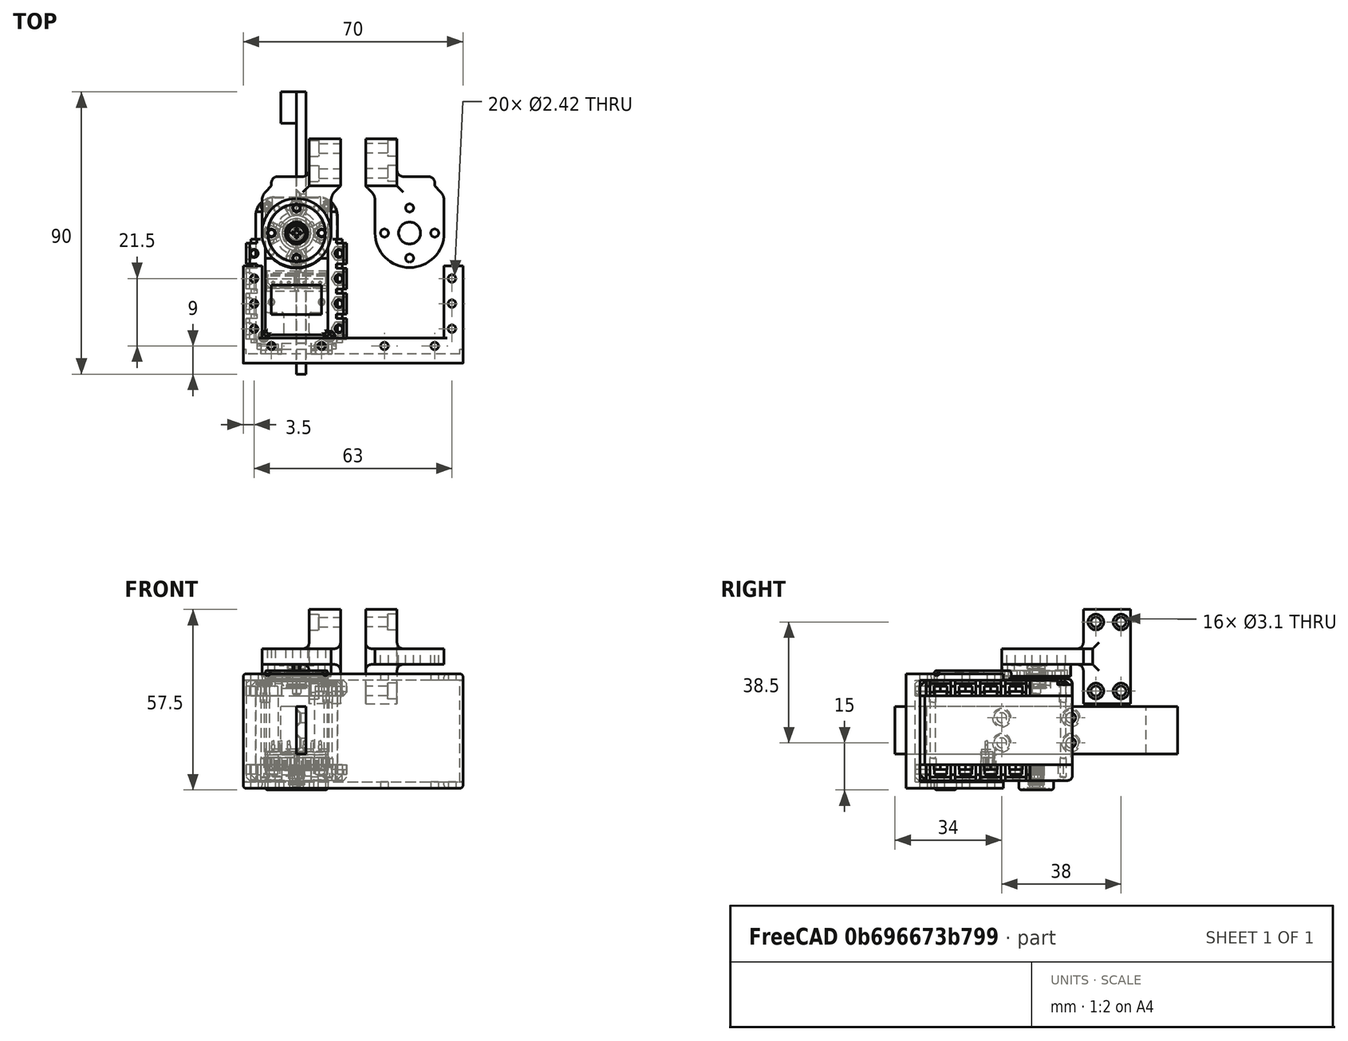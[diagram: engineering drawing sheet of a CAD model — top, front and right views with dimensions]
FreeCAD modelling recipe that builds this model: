
FCSTD DOCUMENT  (FreeCAD 1.1R20260414 (Git shallow))
Label: Unnamed
License: All rights reserved
LicenseURL: https://en.wikipedia.org/wiki/All_rights_reserved
objects: Sketcher::SketchObject×26, Part::Feature×22, PartDesign::Pad×16, App::Point×10, PartDesign::Hole×9, App::Link×8, PartDesign::Fillet×7, App::FeaturePython×7, PartDesign::Body×5, App::Part×4, PartDesign::ShapeBinder×3, PartDesign::PolarPattern×2, PartDesign::Pocket×1, Assembly::JointGroup×1, Assembly::AssemblyObject×1
note: 185 computed .brp shape members not serialized (recipe doc carries the construction recipe); baked Part::Feature solids carry a one-line shape summary decoded from their .brp
EXTERNAL_REF file=../card/Unnamed1.FCStd obj=Body

FEATURE [Part::Feature] Part__Feature  label="PRT0001"
  shape: bbox 32 x 50.5 x 38 mm, 671 faces (baked)
FEATURE [Part::Feature] Part__Feature001  label="PRT0002"
  Placement = pos=(0,0,-2) rot=(0,0,1;3.14159rad)
  shape: bbox 7.033 x 7.036 x 5.513 mm, 32 faces (baked)
FEATURE [Part::Feature] Part__Feature002  label="PRT0003"
  Placement = pos=(9.5,8.5,14.5) rot=(0,0.707107,0.707107;3.14159rad)
  shape: bbox 4.1 x 4.088 x 30.71 mm, 30 faces (baked)
FEATURE [Part::Feature] Part__Feature003  label="PRT0004"
  Placement = pos=(-9.5,8.5,14.5) rot=(0,0.707107,0.707107;3.14159rad)
  shape: bbox 4.1 x 4.088 x 30.71 mm, 30 faces (baked)
FEATURE [Part::Feature] Part__Feature004  label="PRT0005"
  Placement = pos=(10.5,-33,14.5) rot=(0,0.707107,0.707107;3.14159rad)
  shape: bbox 4.1 x 4.088 x 30.71 mm, 30 faces (baked)
FEATURE [Part::Feature] Part__Feature005  label="PRT0006"
  Placement = pos=(-10.5,-33,14.5) rot=(0,0.707107,0.707107;3.14159rad)
  shape: bbox 4.1 x 4.088 x 30.71 mm, 30 faces (baked)
FEATURE [Part::Feature] Part__Feature006  label="PRT0007"
  Placement = pos=(5.05,-15.19,-9.75) rot=(-1,0,0;1.5708rad)
  shape: bbox 9.902 x 4.902 x 9.405 mm, 93 faces (baked)
FEATURE [Part::Feature] Part__Feature007  label="PRT0008"
  Placement = pos=(-4.95,-15.19,-9.75) rot=(-1,0,0;1.5708rad)
  shape: bbox 9.902 x 4.902 x 9.405 mm, 93 faces (baked)
FEATURE [Part::Feature] Part__Feature008  label="PRT0009"
  Placement = pos=(0,0,-18.4) rot=(0,0.707107,0.707107;3.14159rad)
  shape: bbox 4.984 x 4.984 x 7 mm, 133 faces (baked)
FEATURE [Part::Feature] Part__Feature009  label="PRT0010"
  Placement = pos=(0,0,19.16) rot=(0,0,1;1.5708rad)
  shape: bbox 22 x 22 x 6.702 mm, 170 faces (baked)
FEATURE [Part::Feature] Part__Feature010  label="PRT0011"
  Placement = pos=(0,0,19.48) rot=(0,0.707107,0.707107;3.14159rad)
  shape: bbox 7.815 x 6.706 x 9.6 mm, 27 faces (baked)
FEATURE [App::Part] ASM0002_ASM
  Group = -> [Part__Feature,Part__Feature001,Part__Feature002,Part__Feature003,Part__Feature004,Part__Feature005,Part__Feature006,Part__Feature007,Part__Feature008,Part__Feature009,Part__Feature010]
  Origin = -> Origin
FEATURE [App::Point] Origin001
  Role = Origin
FEATURE [App::Part] ASM0001_ASM
  Group = -> [ASM0002_ASM]
  Origin = -> Origin002
FEATURE [App::Point] Origin003
  Role = Origin
FEATURE [App::Point] Origin005  label="Origin006"
  Role = Origin
FEATURE [PartDesign::ShapeBinder] CopyPart__Feature009
  Placement = pos=(0,0,19.16) rot=(0,0,1;1.5708rad)
  TraceSupport = false
FEATURE [Sketcher::SketchObject] Sketch
  ArcFitTolerance = 1e-06
  AttachmentSupport = -> [CopyPart__Feature009]
  ExternalTypes = [0]
  FullyConstrained = true
  MakeInternals = false
  MapMode = 5
  Placement = pos=(0,0,21) rot=(0,0,1;1.5708rad)
  _ExternalGeoVersion = 1
  sketch-geometry (4):
    g0: LineSegment StartX=-2e-15 StartY=-11 StartZ=0 EndX=12 EndY=-11 EndZ=0
    g1: LineSegment StartX=12 StartY=-11 StartZ=0 EndX=12 EndY=11 EndZ=0
    g2: LineSegment StartX=12 StartY=11 StartZ=0 EndX=-3.6e-15 EndY=11 EndZ=0
    g3: ArcOfCircle CenterX=0 CenterY=5e-16 CenterZ=0 NormalX=0 NormalY=0 NormalZ=1 AngleXU=0 Radius=11 StartAngle=1.5708 EndAngle=4.71239
  constraints (12):
    c: Coincident(g0,g1)
    c: Coincident(g1,g2)
    c: Horizontal(g0)
    c: Horizontal(g2)
    c: Vertical(g1)
    c: Distance(g1,g0) = 12
    c: Distance(g0,g2) = 22
    c: PointOnObject(g0,g-2)
    c: Distance(g-1,g0) = 11
    c: Tangent(g0,g3) = -1.5708
    c: Coincident(g3,g2)
    c: Angle(g3) = 3.14159
FEATURE [PartDesign::Pad] Pad
  Direction = (0,0,1)
  Length = 5
  Length2 = 10
  Placement = pos=(0,0,19.16) rot=(0,0,1;1.5708rad)
  Profile = -> Sketch
  ReferenceAxis = -> Sketch [N_Axis]
  Refine = true
  SideType = 0
  Suppressed = false
  Type = 0
  Type2 = 0
FEATURE [Sketcher::SketchObject] Sketch001
  ArcFitTolerance = 1e-06
  AttachmentSupport = -> [Pad]
  ExternalTypes = [0]
  FullyConstrained = true
  MakeInternals = false
  MapMode = 5
  Placement = pos=(0,0,26) rot=(0,0,1;1.5708rad)
  _ExternalGeoVersion = 1
  sketch-geometry (1):
    g0: Circle CenterX=-8 CenterY=0 CenterZ=0 NormalX=0 NormalY=0 NormalZ=1 AngleXU=0 Radius=1.1
  constraints (3):
    c: Diameter(g0) = 2.2
    c: PointOnObject(g0,g-1)
    c: Distance(g0,g-2) = 8
FEATURE [PartDesign::Hole] Hole
  BaseFeature = -> Pad
  BaseProfileType = 7
  CustomThreadClearance = 0
  Depth = 5
  DepthType = 0
  Diameter = 2.552
  DrillForDepth = false
  DrillPoint = 1
  DrillPointAngle = 118
  HoleCutCountersinkAngle = 90
  HoleCutCustomValues = false
  HoleCutDepth = 0
  HoleCutDiameter = 0
  HoleCutType = 0
  ModelThread = false
  Placement = pos=(0,0,19.16) rot=(0,0,1;1.5708rad)
  Profile = -> Sketch001
  Refine = true
  Suppressed = false
  Tapered = false
  TaperedAngle = 90
  ThreadClass = 0
  ThreadDepth = 5
  ThreadDepthType = 0
  ThreadDiameter = 2.2
  ThreadDirection = 0
  ThreadFit = 2
  ThreadSize = 7
  ThreadType = 1
  Threaded = false
  UseCustomThreadClearance = false
FEATURE [PartDesign::PolarPattern] PolarPattern
  Angle = 360
  Axis = -> Sketch001 [N_Axis]
  BaseFeature = -> Hole
  Mode = 0
  Occurrences = 4
  Offset = 120
  Originals = -> [Hole]
  Placement = pos=(0,0,19.16) rot=(0,0,1;1.5708rad)
  Refine = true
  SpacingPattern = [0]
  Spacings = [-1,-1,-1]
  Suppressed = false
  TransformMode = 0
FEATURE [Sketcher::SketchObject] Sketch002
  ArcFitTolerance = 1e-06
  AttachmentSupport = -> [PolarPattern]
  ExternalTypes = [0]
  FullyConstrained = true
  MakeInternals = false
  MapMode = 5
  Placement = pos=(0,0,26) rot=(0,0,1;1.5708rad)
  _ExternalGeoVersion = 1
  sketch-geometry (1):
    g0: Circle CenterX=0 CenterY=0 CenterZ=0 NormalX=0 NormalY=0 NormalZ=1 AngleXU=0 Radius=3
  constraints (2):
    c: Diameter(g0) = 6
    c: Coincident(g0,g-1)
FEATURE [PartDesign::Hole] Hole001
  BaseFeature = -> PolarPattern
  BaseProfileType = 7
  CustomThreadClearance = 0
  Depth = 5
  DepthType = 0
  Diameter = 7
  DrillForDepth = false
  DrillPoint = 1
  DrillPointAngle = 118
  HoleCutCountersinkAngle = 90
  HoleCutCustomValues = false
  HoleCutDepth = 0
  HoleCutDiameter = 0
  HoleCutType = 0
  ModelThread = false
  Placement = pos=(0,0,19.16) rot=(0,0,1;1.5708rad)
  Profile = -> Sketch002
  Refine = true
  Suppressed = false
  Tapered = false
  TaperedAngle = 90
  ThreadClass = 0
  ThreadDepth = 5
  ThreadDepthType = 0
  ThreadDiameter = 6
  ThreadDirection = 0
  ThreadFit = 2
  ThreadSize = 14
  ThreadType = 1
  Threaded = false
  UseCustomThreadClearance = false
FEATURE [App::Point] Origin007  label="Origin009"
  Role = Origin
FEATURE [App::Point] Origin009  label="Origin011"
  Role = Origin
FEATURE [Part::Feature] Part__Feature011  label="PRT0012"
  shape: bbox 32 x 50.5 x 38 mm, 671 faces (baked)
FEATURE [Part::Feature] Part__Feature012  label="PRT0013"
  Placement = pos=(0,0,-2) rot=(0,0,1;3.14159rad)
  shape: bbox 7.033 x 7.036 x 5.513 mm, 32 faces (baked)
FEATURE [Part::Feature] Part__Feature013  label="PRT0014"
  Placement = pos=(9.5,8.5,14.5) rot=(0,0.707107,0.707107;3.14159rad)
  shape: bbox 4.1 x 4.088 x 30.71 mm, 30 faces (baked)
FEATURE [Part::Feature] Part__Feature014  label="PRT0015"
  Placement = pos=(-9.5,8.5,14.5) rot=(0,0.707107,0.707107;3.14159rad)
  shape: bbox 4.1 x 4.088 x 30.71 mm, 30 faces (baked)
FEATURE [Part::Feature] Part__Feature015  label="PRT0016"
  Placement = pos=(10.5,-33,14.5) rot=(0,0.707107,0.707107;3.14159rad)
  shape: bbox 4.1 x 4.088 x 30.71 mm, 30 faces (baked)
FEATURE [Part::Feature] Part__Feature016  label="PRT0017"
  Placement = pos=(-10.5,-33,14.5) rot=(0,0.707107,0.707107;3.14159rad)
  shape: bbox 4.1 x 4.088 x 30.71 mm, 30 faces (baked)
FEATURE [Part::Feature] Part__Feature017  label="PRT0018"
  Placement = pos=(5.05,-15.19,-9.75) rot=(-1,0,0;1.5708rad)
  shape: bbox 9.902 x 4.902 x 9.405 mm, 93 faces (baked)
FEATURE [Part::Feature] Part__Feature018  label="PRT0019"
  Placement = pos=(-4.95,-15.19,-9.75) rot=(-1,0,0;1.5708rad)
  shape: bbox 9.902 x 4.902 x 9.405 mm, 93 faces (baked)
FEATURE [Part::Feature] Part__Feature019  label="PRT0020"
  Placement = pos=(0,0,-18.4) rot=(0,0.707107,0.707107;3.14159rad)
  shape: bbox 4.984 x 4.984 x 7 mm, 133 faces (baked)
FEATURE [Part::Feature] Part__Feature020  label="PRT0021"
  Placement = pos=(0,0,19.16) rot=(0,0,1;1.5708rad)
  shape: bbox 22 x 22 x 6.702 mm, 170 faces (baked)
FEATURE [Part::Feature] Part__Feature021  label="PRT0022"
  Placement = pos=(0,0,19.48) rot=(0,0.707107,0.707107;3.14159rad)
  shape: bbox 7.815 x 6.706 x 9.6 mm, 27 faces (baked)
FEATURE [App::Part] ASM0002_ASM001
  Group = -> [Part__Feature011,Part__Feature012,Part__Feature013,Part__Feature014,Part__Feature015,Part__Feature016,Part__Feature017,Part__Feature018,Part__Feature019,Part__Feature020,Part__Feature021]
  Origin = -> Origin006
FEATURE [App::Part] ASM0001_ASM001
  Group = -> [ASM0002_ASM001]
  Origin = -> Origin008
  Placement = pos=(36,0,0) rot=(0,0,1;0rad)
FEATURE [PartDesign::ShapeBinder] CopyPart__Feature
  TraceSupport = false
FEATURE [App::Point] Origin013  label="Origin015"
  Role = Origin
FEATURE [Sketcher::SketchObject] Sketch012
  ArcFitTolerance = 1e-06
  AttachmentSupport = -> [CopyPart__Feature]
  ExternalTypes = [0]
  FullyConstrained = true
  MakeInternals = false
  MapMode = 5
  Placement = pos=(0,-38.5,0) rot=(1,0,0;1.5708rad)
  _ExternalGeoVersion = 1
  sketch-geometry (4):
    g0: LineSegment StartX=-17 StartY=18 StartZ=0 EndX=-17 EndY=-18.5 EndZ=0
    g1: LineSegment StartX=-17 StartY=-18.5 StartZ=0 EndX=53 EndY=-18.5 EndZ=0
    g2: LineSegment StartX=53 StartY=-18.5 StartZ=0 EndX=53 EndY=18 EndZ=0
    g3: LineSegment StartX=53 StartY=18 StartZ=0 EndX=-17 EndY=18 EndZ=0
  constraints (12):
    c: Coincident(g0,g1)
    c: Coincident(g1,g2)
    c: Coincident(g2,g3)
    c: Coincident(g3,g0)
    c: Vertical(g0)
    c: Vertical(g2)
    c: Horizontal(g1)
    c: Horizontal(g3)
    c: DistanceY(g0,g0) = 36.5
    c: Distance(g-2,g0) = 17
    c: DistanceX(g1,g1) = 70
    c: Distance(g-1,g3) = 18
FEATURE [PartDesign::Pad] Pad006
  Direction = (0,-1,2e-16)
  Length = 3
  Length2 = 10
  Profile = -> Sketch012
  ReferenceAxis = -> Sketch012 [N_Axis]
  Refine = true
  SideType = 0
  Suppressed = false
  Type = 0
  Type2 = 0
FEATURE [Sketcher::SketchObject] Sketch013
  ArcFitTolerance = 1e-06
  AttachmentSupport = -> [Pad006]
  ExternalTypes = [0]
  FullyConstrained = true
  MakeInternals = false
  MapMode = 5
  Placement = pos=(0,-38.5,1.5e-14) rot=(0,0.707107,0.707107;3.14159rad)
  _ExternalGeoVersion = 1
  sketch-geometry (4):
    g0: LineSegment StartX=17 StartY=18 StartZ=0 EndX=-53 EndY=18 EndZ=0
    g1: LineSegment StartX=-53 StartY=18 StartZ=0 EndX=-53 EndY=16 EndZ=0
    g2: LineSegment StartX=-53 StartY=16 StartZ=0 EndX=17 EndY=16 EndZ=0
    g3: LineSegment StartX=17 StartY=16 StartZ=0 EndX=17 EndY=18 EndZ=0
  constraints (12):
    c: Coincident(g0,g1)
    c: Coincident(g1,g2)
    c: Coincident(g2,g3)
    c: Coincident(g3,g0)
    c: Horizontal(g0)
    c: Horizontal(g2)
    c: Vertical(g1)
    c: Vertical(g3)
    c: Distance(g1,g3) = 70
    c: Distance(g0,g2) = 2
    c: Distance(g-1,g2) = 16
    c: Distance(g-2,g3) = 17
FEATURE [PartDesign::Pad] Pad007
  BaseFeature = -> Pad006
  Direction = (0,1,-2e-16)
  Length = 5
  Length2 = 10
  Profile = -> Sketch013
  ReferenceAxis = -> Sketch013 [N_Axis]
  Refine = true
  SideType = 0
  Suppressed = false
  Type = 0
  Type2 = 0
FEATURE [Sketcher::SketchObject] Sketch014
  ArcFitTolerance = 1e-06
  AttachmentSupport = -> [Pad007]
  ExternalTypes = [0]
  FullyConstrained = true
  MakeInternals = false
  MapMode = 5
  Placement = pos=(0,-38.5,1.5e-14) rot=(0,0.707107,0.707107;3.14159rad)
  _ExternalGeoVersion = 1
  sketch-geometry (4):
    g0: LineSegment StartX=17 StartY=-18.5 StartZ=0 EndX=17 EndY=-16.5 EndZ=0
    g1: LineSegment StartX=17 StartY=-16.5 StartZ=0 EndX=-53 EndY=-16.5 EndZ=0
    g2: LineSegment StartX=-53 StartY=-16.5 StartZ=0 EndX=-53 EndY=-18.5 EndZ=0
    g3: LineSegment StartX=-53 StartY=-18.5 StartZ=0 EndX=17 EndY=-18.5 EndZ=0
  constraints (12):
    c: Coincident(g0,g1)
    c: Coincident(g1,g2)
    c: Coincident(g2,g3)
    c: Coincident(g3,g0)
    c: Vertical(g0)
    c: Vertical(g2)
    c: Horizontal(g1)
    c: Horizontal(g3)
    c: Distance(g0,g2) = 70
    c: Distance(g1,g3) = 2
    c: Distance(g-2,g0) = 17
    c: Distance(g-1,g3) = 18.5
FEATURE [PartDesign::Pad] Pad008
  BaseFeature = -> Pad007
  Direction = (0,1,-2e-16)
  Length = 5
  Length2 = 10
  Profile = -> Sketch014
  ReferenceAxis = -> Sketch014 [N_Axis]
  Refine = true
  SideType = 0
  Suppressed = false
  Type = 0
  Type2 = 0
FEATURE [Sketcher::SketchObject] Sketch015
  ArcFitTolerance = 1e-06
  AttachmentSupport = -> [Pad008]
  ExternalTypes = [0,0]
  FullyConstrained = true
  MakeInternals = false
  MapMode = 5
  Placement = pos=(0,-33.5,1.19e-13) rot=(0,0.707107,0.707107;3.14159rad)
  _ExternalGeoVersion = 1
  sketch-geometry (16):
    g0: LineSegment StartX=17 StartY=16 StartZ=0 EndX=17 EndY=18 EndZ=0
    g1: LineSegment StartX=17 StartY=18 StartZ=0 EndX=11 EndY=18 EndZ=0
    g2: LineSegment StartX=11 StartY=18 StartZ=0 EndX=11 EndY=16 EndZ=0
    g3: LineSegment StartX=11 StartY=16 StartZ=0 EndX=17 EndY=16 EndZ=0
    g4: LineSegment StartX=-53 StartY=16 StartZ=0 EndX=-47 EndY=16 EndZ=0
    g5: LineSegment StartX=-47 StartY=16 StartZ=0 EndX=-47 EndY=18 EndZ=0
    g6: LineSegment StartX=-47 StartY=18 StartZ=0 EndX=-53 EndY=18 EndZ=0
    g7: LineSegment StartX=-53 StartY=18 StartZ=0 EndX=-53 EndY=16 EndZ=0
    g8: LineSegment StartX=-53 StartY=-16.5 StartZ=0 EndX=-53 EndY=-18.5 EndZ=0
    g9: LineSegment StartX=-53 StartY=-18.5 StartZ=0 EndX=-47 EndY=-18.5 EndZ=0
    g10: LineSegment StartX=-47 StartY=-18.5 StartZ=0 EndX=-47 EndY=-16.5 EndZ=0
    g11: LineSegment StartX=-47 StartY=-16.5 StartZ=0 EndX=-53 EndY=-16.5 EndZ=0
    g12: LineSegment StartX=17 StartY=-16.5 StartZ=0 EndX=11 EndY=-16.5 EndZ=0
    g13: LineSegment StartX=11 StartY=-16.5 StartZ=0 EndX=11 EndY=-18.5 EndZ=0
    g14: LineSegment StartX=11 StartY=-18.5 StartZ=0 EndX=17 EndY=-18.5 EndZ=0
    g15: LineSegment StartX=17 StartY=-18.5 StartZ=0 EndX=17 EndY=-16.5 EndZ=0
  constraints (48):
    c: Coincident(g0,g1)
    c: Coincident(g1,g2)
    c: Coincident(g2,g3)
    c: Coincident(g3,g0)
    c: Vertical(g0)
    c: Vertical(g2)
    c: Horizontal(g1)
    c: Horizontal(g3)
    c: Distance(g0,g2) = 6
    c: Distance(g1,g3) = 2
    c: Distance(g-1,g3) = 16
    c: Distance(g-2,g0) = 17
    c: Coincident(g4,g5)
    c: Coincident(g5,g6)
    c: Coincident(g6,g7)
    c: Coincident(g7,g4)
    c: Horizontal(g4)
    c: Horizontal(g6)
    c: Vertical(g5)
    c: Vertical(g7)
    c: Distance(g-1,g4) = 16
    c: Distance(g7,g7) = 2
    c: Distance(g-2,g7) = 53
    c: Distance(g6,g6) = 6
    c: Coincident(g8,g9)
    c: Coincident(g9,g10)
    c: Coincident(g10,g11)
    c: Coincident(g11,g8)
    c: Vertical(g8)
    c: Vertical(g10)
    c: Horizontal(g9)
    c: Horizontal(g11)
    c: Coincident(g12,g13)
    c: Coincident(g13,g14)
    c: Coincident(g14,g15)
    c: Coincident(g15,g12)
    c: Horizontal(g12)
    c: Horizontal(g14)
    c: Vertical(g13)
    c: Vertical(g15)
    c: Distance(g-2,g15) = 17
    c: Distance(g-1,g12) = 16.5
    c: Distance(g13,g13) = 2
    c: Distance(g14,g14) = 6
    c: Distance(g-1,g11) = 16.5
    c: Distance(g-2,g8) = 53
    c: Distance(g9,g9) = 6
    c: Distance(g10,g10) = 2
FEATURE [PartDesign::Pad] Pad009
  BaseFeature = -> Pad008
  Direction = (0,1,-3.6e-15)
  Length = 23
  Length2 = 10
  Profile = -> Sketch015
  ReferenceAxis = -> Sketch015 [N_Axis]
  Refine = true
  SideType = 0
  Suppressed = false
  Type = 0
  Type2 = 0
FEATURE [Sketcher::SketchObject] Sketch016
  ArcFitTolerance = 1e-06
  AttachmentSupport = -> [Pad009]
  ExternalTypes = [0,0]
  FullyConstrained = true
  MakeInternals = false
  MapMode = 5
  Placement = pos=(0,-38.5,1.5e-14) rot=(0,0.707107,0.707107;3.14159rad)
  _ExternalGeoVersion = 1
  sketch-geometry (8):
    g0: LineSegment StartX=-53 StartY=16 StartZ=0 EndX=-53 EndY=-16.5 EndZ=0
    g1: LineSegment StartX=-53 StartY=-16.5 StartZ=0 EndX=-52 EndY=-16.5 EndZ=0
    g2: LineSegment StartX=-52 StartY=-16.5 StartZ=0 EndX=-52 EndY=16 EndZ=0
    g3: LineSegment StartX=-52 StartY=16 StartZ=0 EndX=-53 EndY=16 EndZ=0
    g4: LineSegment StartX=17 StartY=16 StartZ=0 EndX=16 EndY=16 EndZ=0
    g5: LineSegment StartX=16 StartY=16 StartZ=0 EndX=16 EndY=-16.5 EndZ=0
    g6: LineSegment StartX=16 StartY=-16.5 StartZ=0 EndX=17 EndY=-16.5 EndZ=0
    g7: LineSegment StartX=17 StartY=-16.5 StartZ=0 EndX=17 EndY=16 EndZ=0
  constraints (24):
    c: Coincident(g0,g1)
    c: Coincident(g1,g2)
    c: Coincident(g2,g3)
    c: Coincident(g3,g0)
    c: Vertical(g0)
    c: Vertical(g2)
    c: Horizontal(g1)
    c: Horizontal(g3)
    c: Distance(g0,g2) = 1
    c: Distance(g1,g3) = 32.5
    c: Distance(g-1,g3) = 16
    c: Distance(g-2,g0) = 53
    c: Coincident(g4,g5)
    c: Coincident(g5,g6)
    c: Coincident(g6,g7)
    c: Coincident(g7,g4)
    c: Horizontal(g4)
    c: Horizontal(g6)
    c: Vertical(g5)
    c: Vertical(g7)
    c: Distance(g-2,g7) = 17
    c: Distance(g-1,g4) = 16
    c: Distance(g7,g7) = 32.5
    c: Distance(g6,g6) = 1
FEATURE [PartDesign::Pad] Pad010
  BaseFeature = -> Pad009
  Direction = (0,1,-2e-16)
  Length = 1.5
  Length2 = 10
  Profile = -> Sketch016
  ReferenceAxis = -> Sketch016 [N_Axis]
  Refine = true
  SideType = 0
  Suppressed = false
  Type = 0
  Type2 = 0
FEATURE [PartDesign::Fillet] Fillet008
  Base = -> Pad010 [Edge47,Edge45,Edge20,Edge18,Edge5,Edge23,Edge41,Edge43]
  BaseFeature = -> Pad010
  Radius = 1
  Refine = true
  SupportTransform = false
  Suppressed = false
  UseAllEdges = false
FEATURE [Sketcher::SketchObject] Sketch017
  ArcFitTolerance = 1e-06
  AttachmentSupport = -> [Fillet008]
  ExternalTypes = [0]
  FullyConstrained = true
  MakeInternals = false
  MapMode = 5
  Placement = pos=(0,-1.22e-14,18) rot=(0,0,1;0rad)
  _ExternalGeoVersion = 1
  sketch-geometry (10):
    g0: Circle CenterX=-13.5 CenterY=-14.5 CenterZ=0 NormalX=0 NormalY=0 NormalZ=1 AngleXU=0 Radius=1.1
    g1: Circle CenterX=-13.5 CenterY=-22.5 CenterZ=0 NormalX=0 NormalY=0 NormalZ=1 AngleXU=0 Radius=1.1
    g2: Circle CenterX=-13.5 CenterY=-30.5 CenterZ=0 NormalX=0 NormalY=0 NormalZ=1 AngleXU=0 Radius=1.1
    g3: Circle CenterX=49.5 CenterY=-14.5 CenterZ=0 NormalX=0 NormalY=0 NormalZ=1 AngleXU=0 Radius=1.1
    g4: Circle CenterX=49.5 CenterY=-22.5 CenterZ=0 NormalX=0 NormalY=0 NormalZ=1 AngleXU=0 Radius=1.1
    g5: Circle CenterX=49.5 CenterY=-30.5 CenterZ=0 NormalX=0 NormalY=0 NormalZ=1 AngleXU=0 Radius=1.1
    g6: Circle CenterX=-8 CenterY=-36 CenterZ=0 NormalX=0 NormalY=0 NormalZ=1 AngleXU=0 Radius=1.1
    g7: Circle CenterX=8 CenterY=-36 CenterZ=0 NormalX=0 NormalY=0 NormalZ=1 AngleXU=0 Radius=1.1
    g8: Circle CenterX=44 CenterY=-36 CenterZ=0 NormalX=0 NormalY=0 NormalZ=1 AngleXU=0 Radius=1.1
    g9: Circle CenterX=28 CenterY=-36 CenterZ=0 NormalX=0 NormalY=0 NormalZ=1 AngleXU=0 Radius=1.1
  constraints (30):
    c: Diameter(g0) = 2.2
    c: Equal(g0,g1)
    c: Equal(g2,g1)
    c: Distance(g0,g-2) = 13.5
    c: DistanceY(g0,g-1) = 14.5
    c: Distance(g1,g0) = 8
    c: Distance(g1,g-2) = 13.5
    c: Distance(g2,g1) = 8
    c: Distance(g2,g-2) = 13.5
    c: Diameter(g3) = 2.2
    c: DistanceX(g-1,g3) = 49.5
    c: DistanceY(g3,g-1) = 14.5
    c: Equal(g3,g4)
    c: Equal(g4,g5)
    c: Distance(g4,g3) = 8
    c: Distance(g5,g4) = 8
    c: Distance(g4,g-2) = 49.5
    c: Distance(g5,g-2) = 49.5
    c: Equal(g2,g6)
    c: Distance(g6,g-2) = 8
    c: DistanceY(g6,g-1) = 36
    c: Equal(g7,g6)
    c: DistanceX(g6,g7) = 16
    c: Distance(g7,g-1) = 36
    c: Equal(g9,g5)
    c: Equal(g8,g5)
    c: DistanceX(g9,g8) = 16
    c: Distance(g9,g-1) = 36
    c: Distance(g8,g-1) = 36
    c: Distance(g9,g-2) = 28
FEATURE [PartDesign::Hole] Hole006
  BaseFeature = -> Fillet008
  BaseProfileType = 7
  CustomThreadClearance = 0
  Depth = 40
  DepthType = 0
  Diameter = 2.42
  DrillForDepth = false
  DrillPoint = 1
  DrillPointAngle = 118
  HoleCutCountersinkAngle = 90
  HoleCutCustomValues = false
  HoleCutDepth = 0
  HoleCutDiameter = 0
  HoleCutType = 0
  ModelThread = false
  Profile = -> Sketch017
  Refine = true
  Suppressed = false
  Tapered = false
  TaperedAngle = 90
  ThreadClass = 0
  ThreadDepth = 40
  ThreadDepthType = 0
  ThreadDiameter = 2.2
  ThreadDirection = 0
  ThreadFit = 0
  ThreadSize = 7
  ThreadType = 1
  Threaded = false
  UseCustomThreadClearance = false
FEATURE [PartDesign::Body] Body002
  AllowCompound = true
  Group = -> [CopyPart__Feature,Sketch012,Pad006,Sketch013,Pad007,Sketch014,Pad008,Sketch015,Pad009,Sketch016,Pad010,Fillet008,Sketch017,Hole006]
  Origin = -> Origin012
  Tip = -> Hole006
FEATURE [Sketcher::SketchObject] Sketch018
  ArcFitTolerance = 1e-06
  AttachmentSupport = -> [Hole001]
  ExternalTypes = [0]
  FullyConstrained = true
  MakeInternals = false
  MapMode = 5
  Placement = pos=(0,0,26) rot=(0,0,1;1.5708rad)
  _ExternalGeoVersion = 1
  sketch-geometry (4):
    g0: LineSegment StartX=12 StartY=11 StartZ=0 EndX=15 EndY=8.00374 EndZ=0
    g1: LineSegment StartX=15 StartY=8.00374 StartZ=0 EndX=15 EndY=-13.9963 EndZ=0
    g2: LineSegment StartX=15 StartY=-13.9963 StartZ=0 EndX=12 EndY=-11 EndZ=0
    g3: LineSegment StartX=12 StartY=11 StartZ=0 EndX=12 EndY=-11 EndZ=0
  constraints (12):
    c: Coincident(g0,g1)
    c: Vertical(g1)
    c: Coincident(g1,g2)
    c: Coincident(g0,g3)
    c: Coincident(g3,g2)
    c: Vertical(g3)
    c: Distance(g1,g1) = 22
    c: Distance(g0,g0) = 4.24
    c: Equal(g1,g3)
    c: Distance(g-2,g1) = 15
    c: Distance(g-2,g3) = 12
    c: Distance(g0,g-1) = 11
FEATURE [PartDesign::Pad] Pad011
  BaseFeature = -> Hole001
  Direction = (0,0,1)
  Length = 5
  Length2 = 10
  Placement = pos=(0,0,19.16) rot=(0,0,1;1.5708rad)
  Profile = -> Sketch018
  ReferenceAxis = -> Sketch018 [N_Axis]
  Refine = true
  Reversed = true
  SideType = 0
  Suppressed = false
  Type = 0
  Type2 = 0
FEATURE [Sketcher::SketchObject] Sketch019
  ArcFitTolerance = 1e-06
  AttachmentSupport = -> [Pad011]
  ExternalTypes = [0,0,0]
  FullyConstrained = true
  MakeInternals = false
  MapMode = 5
  Placement = pos=(0,0,26) rot=(0,0,1;1.5708rad)
  _ExternalGeoVersion = 1
  sketch-geometry (4):
    g0: LineSegment StartX=15 StartY=8 StartZ=0 EndX=15 EndY=-14 EndZ=0
    g1: LineSegment StartX=15 StartY=-14 StartZ=0 EndX=18 EndY=-14 EndZ=0
    g2: LineSegment StartX=18 StartY=-14 StartZ=0 EndX=18 EndY=8 EndZ=0
    g3: LineSegment StartX=18 StartY=8 StartZ=0 EndX=15 EndY=8 EndZ=0
  constraints (12):
    c: Coincident(g0,g1)
    c: Coincident(g1,g2)
    c: Coincident(g2,g3)
    c: Coincident(g3,g0)
    c: Vertical(g0)
    c: Vertical(g2)
    c: Horizontal(g1)
    c: Horizontal(g3)
    c: Distance(g0,g2) = 3
    c: Distance(g1,g3) = 22
    c: Distance(g-2,g2) = 18
    c: Distance(g1,g-1) = 14
FEATURE [PartDesign::Pad] Pad012
  BaseFeature = -> Pad011
  Direction = (0,0,1)
  Length = 5
  Length2 = 10
  Placement = pos=(0,0,19.16) rot=(0,0,1;1.5708rad)
  Profile = -> Sketch019
  ReferenceAxis = -> Sketch019 [N_Axis]
  Refine = true
  Reversed = true
  SideType = 0
  Suppressed = false
  Type = 0
  Type2 = 0
FEATURE [Sketcher::SketchObject] Sketch020
  ArcFitTolerance = 1e-06
  AttachmentSupport = -> [Pad012]
  ExternalTypes = [0]
  FullyConstrained = true
  MakeInternals = false
  MapMode = 5
  Placement = pos=(14,-4.7e-15,19.16) rot=(0.57735,0.57735,0.57735;2.0944rad)
  _ExternalGeoVersion = 1
  sketch-geometry (4):
    g0: LineSegment StartX=15 StartY=19.34 StartZ=0 EndX=15 EndY=-10.66 EndZ=0
    g1: LineSegment StartX=15 StartY=-10.66 StartZ=0 EndX=30 EndY=-10.66 EndZ=0
    g2: LineSegment StartX=30 StartY=-10.66 StartZ=0 EndX=30 EndY=19.34 EndZ=0
    g3: LineSegment StartX=30 StartY=19.34 StartZ=0 EndX=15 EndY=19.34 EndZ=0
  constraints (12):
    c: Coincident(g0,g1)
    c: Coincident(g1,g2)
    c: Coincident(g2,g3)
    c: Coincident(g3,g0)
    c: Vertical(g0)
    c: Vertical(g2)
    c: Horizontal(g1)
    c: Horizontal(g3)
    c: Distance(g0,g2) = 15
    c: Distance(g1,g3) = 30
    c: Distance(g-1,g1) = 10.66
    c: Distance(g-2,g0) = 15
FEATURE [PartDesign::Pad] Pad013
  BaseFeature = -> Pad012
  Direction = (1,0,0)
  Length = 10
  Length2 = 10
  Placement = pos=(0,0,19.16) rot=(0,0,1;1.5708rad)
  Profile = -> Sketch020
  ReferenceAxis = -> Sketch020 [N_Axis]
  Refine = true
  Reversed = true
  SideType = 0
  Suppressed = false
  Type = 0
  Type2 = 0
FEATURE [PartDesign::Fillet] Fillet
  Base = -> Pad013 [Edge42,Edge40,Edge28,Edge12]
  BaseFeature = -> Pad013
  Placement = pos=(0,0,19.16) rot=(0,0,1;1.5708rad)
  Radius = 2
  Refine = true
  SupportTransform = false
  Suppressed = false
  UseAllEdges = false
FEATURE [PartDesign::Fillet] Fillet009
  Base = -> Fillet [Edge31,Edge29,Edge6,Edge4]
  BaseFeature = -> Fillet
  Placement = pos=(0,0,19.16) rot=(0,0,1;1.5708rad)
  Radius = 2
  Refine = true
  SupportTransform = false
  Suppressed = false
  UseAllEdges = false
FEATURE [PartDesign::Fillet] Fillet010
  Base = -> Fillet009 [Edge29,Edge19]
  BaseFeature = -> Fillet009
  Placement = pos=(0,0,19.16) rot=(0,0,1;1.5708rad)
  Radius = 4
  Refine = true
  SupportTransform = false
  Suppressed = false
  UseAllEdges = false
FEATURE [Sketcher::SketchObject] Sketch021
  ArcFitTolerance = 1e-06
  AttachmentSupport = -> [Fillet010]
  ExternalTypes = [0,0,0]
  FullyConstrained = true
  MakeInternals = false
  MapMode = 5
  Placement = pos=(4,-4e-16,19.16) rot=(0.57735,-0.57735,-0.57735;2.0944rad)
  _ExternalGeoVersion = 1
  sketch-geometry (4):
    g0: Circle CenterX=-19 CenterY=15.34 CenterZ=0 NormalX=0 NormalY=0 NormalZ=1 AngleXU=0 Radius=1.1
    g1: Circle CenterX=-27 CenterY=15.34 CenterZ=0 NormalX=0 NormalY=0 NormalZ=1 AngleXU=0 Radius=1.1
    g2: Circle CenterX=-19 CenterY=-6.66 CenterZ=0 NormalX=0 NormalY=0 NormalZ=1 AngleXU=0 Radius=1.1
    g3: Circle CenterX=-27 CenterY=-6.66 CenterZ=0 NormalX=0 NormalY=0 NormalZ=1 AngleXU=0 Radius=1.1
  constraints (12):
    c: Diameter(g0) = 2.2
    c: Equal(g1,g0)
    c: Equal(g3,g1)
    c: Equal(g2,g3)
    c: DistanceX(g1,g0) = 8
    c: DistanceX(g3,g2) = 8
    c: Distance(g0,g-1) = 15.34
    c: Distance(g0,g-2) = 19
    c: Distance(g1,g-1) = 15.34
    c: Distance(g2,g-2) = 19
    c: Distance(g2,g-1) = 6.66
    c: Distance(g3,g-1) = 6.66
FEATURE [PartDesign::Hole] Hole007
  BaseFeature = -> Fillet010
  BaseProfileType = 7
  CustomThreadClearance = 0
  Depth = 10
  DepthType = 0
  Diameter = 3.1
  DrillForDepth = false
  DrillPoint = 0
  DrillPointAngle = 118
  HoleCutCountersinkAngle = 90
  HoleCutCustomValues = false
  HoleCutDepth = 3
  HoleCutDiameter = 5
  HoleCutType = 1
  ModelThread = false
  Placement = pos=(0,0,19.16) rot=(0,0,1;1.5708rad)
  Profile = -> Sketch021
  Refine = true
  Suppressed = false
  Tapered = false
  TaperedAngle = 90
  ThreadClass = 0
  ThreadDepth = 10
  ThreadDepthType = 0
  ThreadDiameter = 2.5
  ThreadDirection = 0
  ThreadFit = 2
  ThreadSize = 8
  ThreadType = 1
  Threaded = false
  UseCustomThreadClearance = false
FEATURE [PartDesign::Body] Body
  AllowCompound = true
  Group = -> [CopyPart__Feature009,Sketch,Pad,Sketch001,Hole,PolarPattern,Sketch002,Hole001,Sketch018,Pad011,Sketch019,Pad012,Sketch020,Pad013,Fillet,Fillet009,Fillet010,Sketch021,Hole007]
  Origin = -> Origin004
  Tip = -> Hole007
FEATURE [PartDesign::ShapeBinder] CopyPart__Feature010
  Placement = pos=(0,0,19.16) rot=(0,0,1;1.5708rad)
  TraceSupport = false
FEATURE [App::Point] Origin015  label="Origin017"
  Role = Origin
FEATURE [Sketcher::SketchObject] Sketch022
  ArcFitTolerance = 1e-06
  AttachmentSupport = -> [CopyPart__Feature010]
  ExternalTypes = [0]
  FullyConstrained = true
  MakeInternals = false
  MapMode = 5
  Placement = pos=(0,0,21) rot=(0,0,1;1.5708rad)
  _ExternalGeoVersion = 1
  sketch-geometry (4):
    g0: LineSegment StartX=-2e-15 StartY=-11 StartZ=0 EndX=12 EndY=-11 EndZ=0
    g1: LineSegment StartX=12 StartY=-11 StartZ=0 EndX=12 EndY=11 EndZ=0
    g2: LineSegment StartX=12 StartY=11 StartZ=0 EndX=-3.6e-15 EndY=11 EndZ=0
    g3: ArcOfCircle CenterX=0 CenterY=5e-16 CenterZ=0 NormalX=0 NormalY=0 NormalZ=1 AngleXU=0 Radius=11 StartAngle=1.5708 EndAngle=4.71239
  constraints (12):
    c: Coincident(g0,g1)
    c: Coincident(g1,g2)
    c: Horizontal(g0)
    c: Horizontal(g2)
    c: Vertical(g1)
    c: Distance(g1,g0) = 12
    c: Distance(g0,g2) = 22
    c: PointOnObject(g0,g-2)
    c: Distance(g-1,g0) = 11
    c: Tangent(g0,g3) = -1.5708
    c: Coincident(g3,g2)
    c: Angle(g3) = 3.14159
FEATURE [PartDesign::Pad] Pad014
  Direction = (0,0,1)
  Length = 5
  Length2 = 10
  Placement = pos=(0,0,19.16) rot=(0,0,1;1.5708rad)
  Profile = -> Sketch022
  ReferenceAxis = -> Sketch022 [N_Axis]
  Refine = true
  SideType = 0
  Suppressed = false
  Type = 0
  Type2 = 0
FEATURE [Sketcher::SketchObject] Sketch023
  ArcFitTolerance = 1e-06
  AttachmentSupport = -> [Pad014]
  ExternalTypes = [0]
  FullyConstrained = true
  MakeInternals = false
  MapMode = 5
  Placement = pos=(0,0,26) rot=(0,0,1;1.5708rad)
  _ExternalGeoVersion = 1
  sketch-geometry (1):
    g0: Circle CenterX=-8 CenterY=0 CenterZ=0 NormalX=0 NormalY=0 NormalZ=1 AngleXU=0 Radius=1.1
  constraints (3):
    c: Diameter(g0) = 2.2
    c: PointOnObject(g0,g-1)
    c: Distance(g0,g-2) = 8
FEATURE [PartDesign::Hole] Hole008
  BaseFeature = -> Pad014
  BaseProfileType = 7
  CustomThreadClearance = 0
  Depth = 5
  DepthType = 0
  Diameter = 2.552
  DrillForDepth = false
  DrillPoint = 1
  DrillPointAngle = 118
  HoleCutCountersinkAngle = 90
  HoleCutCustomValues = false
  HoleCutDepth = 0
  HoleCutDiameter = 0
  HoleCutType = 0
  ModelThread = false
  Placement = pos=(0,0,19.16) rot=(0,0,1;1.5708rad)
  Profile = -> Sketch023
  Refine = true
  Suppressed = false
  Tapered = false
  TaperedAngle = 90
  ThreadClass = 0
  ThreadDepth = 5
  ThreadDepthType = 0
  ThreadDiameter = 2.2
  ThreadDirection = 0
  ThreadFit = 2
  ThreadSize = 7
  ThreadType = 1
  Threaded = false
  UseCustomThreadClearance = false
FEATURE [PartDesign::PolarPattern] PolarPattern001
  Angle = 360
  Axis = -> Sketch023 [N_Axis]
  BaseFeature = -> Hole008
  Mode = 0
  Occurrences = 4
  Offset = 120
  Originals = -> [Hole008]
  Placement = pos=(0,0,19.16) rot=(0,0,1;1.5708rad)
  Refine = true
  SpacingPattern = [0]
  Spacings = [-1,-1,-1]
  Suppressed = false
  TransformMode = 0
FEATURE [Sketcher::SketchObject] Sketch024
  ArcFitTolerance = 1e-06
  AttachmentSupport = -> [PolarPattern001]
  ExternalTypes = [0]
  FullyConstrained = true
  MakeInternals = false
  MapMode = 5
  Placement = pos=(0,0,26) rot=(0,0,1;1.5708rad)
  _ExternalGeoVersion = 1
  sketch-geometry (1):
    g0: Circle CenterX=0 CenterY=0 CenterZ=0 NormalX=0 NormalY=0 NormalZ=1 AngleXU=0 Radius=3
  constraints (2):
    c: Diameter(g0) = 6
    c: Coincident(g0,g-1)
FEATURE [PartDesign::Hole] Hole009
  BaseFeature = -> PolarPattern001
  BaseProfileType = 7
  CustomThreadClearance = 0
  Depth = 5
  DepthType = 0
  Diameter = 7
  DrillForDepth = false
  DrillPoint = 1
  DrillPointAngle = 118
  HoleCutCountersinkAngle = 90
  HoleCutCustomValues = false
  HoleCutDepth = 0
  HoleCutDiameter = 0
  HoleCutType = 0
  ModelThread = false
  Placement = pos=(0,0,19.16) rot=(0,0,1;1.5708rad)
  Profile = -> Sketch024
  Refine = true
  Suppressed = false
  Tapered = false
  TaperedAngle = 90
  ThreadClass = 0
  ThreadDepth = 5
  ThreadDepthType = 0
  ThreadDiameter = 6
  ThreadDirection = 0
  ThreadFit = 2
  ThreadSize = 14
  ThreadType = 1
  Threaded = false
  UseCustomThreadClearance = false
FEATURE [Sketcher::SketchObject] Sketch025
  ArcFitTolerance = 1e-06
  AttachmentSupport = -> [Hole009]
  ExternalTypes = [0]
  FullyConstrained = true
  MakeInternals = false
  MapMode = 5
  Placement = pos=(0,0,26) rot=(0,0,1;1.5708rad)
  _ExternalGeoVersion = 1
  sketch-geometry (4):
    g0: LineSegment StartX=12 StartY=11 StartZ=0 EndX=15 EndY=8.00374 EndZ=0
    g1: LineSegment StartX=15 StartY=8.00374 StartZ=0 EndX=15 EndY=-13.9963 EndZ=0
    g2: LineSegment StartX=15 StartY=-13.9963 StartZ=0 EndX=12 EndY=-11 EndZ=0
    g3: LineSegment StartX=12 StartY=11 StartZ=0 EndX=12 EndY=-11 EndZ=0
  constraints (12):
    c: Coincident(g0,g1)
    c: Vertical(g1)
    c: Coincident(g1,g2)
    c: Coincident(g0,g3)
    c: Coincident(g3,g2)
    c: Vertical(g3)
    c: Distance(g1,g1) = 22
    c: Distance(g0,g0) = 4.24
    c: Equal(g1,g3)
    c: Distance(g-2,g1) = 15
    c: Distance(g-2,g3) = 12
    c: Distance(g0,g-1) = 11
FEATURE [PartDesign::Pad] Pad015
  BaseFeature = -> Hole009
  Direction = (0,0,1)
  Length = 5
  Length2 = 10
  Placement = pos=(0,0,19.16) rot=(0,0,1;1.5708rad)
  Profile = -> Sketch025
  ReferenceAxis = -> Sketch025 [N_Axis]
  Refine = true
  Reversed = true
  SideType = 0
  Suppressed = false
  Type = 0
  Type2 = 0
FEATURE [Sketcher::SketchObject] Sketch026
  ArcFitTolerance = 1e-06
  AttachmentSupport = -> [Pad015]
  ExternalTypes = [0,0,0]
  FullyConstrained = true
  MakeInternals = false
  MapMode = 5
  Placement = pos=(0,0,26) rot=(0,0,1;1.5708rad)
  _ExternalGeoVersion = 1
  sketch-geometry (4):
    g0: LineSegment StartX=15 StartY=8 StartZ=0 EndX=15 EndY=-14 EndZ=0
    g1: LineSegment StartX=15 StartY=-14 StartZ=0 EndX=18 EndY=-14 EndZ=0
    g2: LineSegment StartX=18 StartY=-14 StartZ=0 EndX=18 EndY=8 EndZ=0
    g3: LineSegment StartX=18 StartY=8 StartZ=0 EndX=15 EndY=8 EndZ=0
  constraints (12):
    c: Coincident(g0,g1)
    c: Coincident(g1,g2)
    c: Coincident(g2,g3)
    c: Coincident(g3,g0)
    c: Vertical(g0)
    c: Vertical(g2)
    c: Horizontal(g1)
    c: Horizontal(g3)
    c: Distance(g0,g2) = 3
    c: Distance(g1,g3) = 22
    c: Distance(g-2,g2) = 18
    c: Distance(g1,g-1) = 14
FEATURE [PartDesign::Pad] Pad016
  BaseFeature = -> Pad015
  Direction = (0,0,1)
  Length = 5
  Length2 = 10
  Placement = pos=(0,0,19.16) rot=(0,0,1;1.5708rad)
  Profile = -> Sketch026
  ReferenceAxis = -> Sketch026 [N_Axis]
  Refine = true
  Reversed = true
  SideType = 0
  Suppressed = false
  Type = 0
  Type2 = 0
FEATURE [Sketcher::SketchObject] Sketch027
  ArcFitTolerance = 1e-06
  AttachmentSupport = -> [Pad016]
  ExternalTypes = [0]
  FullyConstrained = true
  MakeInternals = false
  MapMode = 5
  Placement = pos=(14,-4.7e-15,19.16) rot=(0.57735,0.57735,0.57735;2.0944rad)
  _ExternalGeoVersion = 1
  sketch-geometry (4):
    g0: LineSegment StartX=15 StartY=19.34 StartZ=0 EndX=15 EndY=-10.66 EndZ=0
    g1: LineSegment StartX=15 StartY=-10.66 StartZ=0 EndX=30 EndY=-10.66 EndZ=0
    g2: LineSegment StartX=30 StartY=-10.66 StartZ=0 EndX=30 EndY=19.34 EndZ=0
    g3: LineSegment StartX=30 StartY=19.34 StartZ=0 EndX=15 EndY=19.34 EndZ=0
  constraints (12):
    c: Coincident(g0,g1)
    c: Coincident(g1,g2)
    c: Coincident(g2,g3)
    c: Coincident(g3,g0)
    c: Vertical(g0)
    c: Vertical(g2)
    c: Horizontal(g1)
    c: Horizontal(g3)
    c: Distance(g0,g2) = 15
    c: Distance(g1,g3) = 30
    c: Distance(g-1,g1) = 10.66
    c: Distance(g-2,g0) = 15
FEATURE [PartDesign::Pad] Pad017
  BaseFeature = -> Pad016
  Direction = (1,0,0)
  Length = 10
  Length2 = 10
  Placement = pos=(0,0,19.16) rot=(0,0,1;1.5708rad)
  Profile = -> Sketch027
  ReferenceAxis = -> Sketch027 [N_Axis]
  Refine = true
  Reversed = true
  SideType = 0
  Suppressed = false
  Type = 0
  Type2 = 0
FEATURE [PartDesign::Fillet] Fillet011
  Base = -> Pad017 [Edge42,Edge40,Edge28,Edge12]
  BaseFeature = -> Pad017
  Placement = pos=(0,0,19.16) rot=(0,0,1;1.5708rad)
  Radius = 2
  Refine = true
  SupportTransform = false
  Suppressed = false
  UseAllEdges = false
FEATURE [PartDesign::Fillet] Fillet012
  Base = -> Fillet011 [Edge31,Edge29,Edge6,Edge4]
  BaseFeature = -> Fillet011
  Placement = pos=(0,0,19.16) rot=(0,0,1;1.5708rad)
  Radius = 2
  Refine = true
  SupportTransform = false
  Suppressed = false
  UseAllEdges = false
FEATURE [PartDesign::Fillet] Fillet013
  Base = -> Fillet012 [Edge29,Edge19]
  BaseFeature = -> Fillet012
  Placement = pos=(0,0,19.16) rot=(0,0,1;1.5708rad)
  Radius = 4
  Refine = true
  SupportTransform = false
  Suppressed = false
  UseAllEdges = false
FEATURE [Sketcher::SketchObject] Sketch028
  ArcFitTolerance = 1e-06
  AttachmentSupport = -> [Fillet013]
  ExternalTypes = [0,0,0]
  FullyConstrained = true
  MakeInternals = false
  MapMode = 5
  Placement = pos=(4,-4e-16,19.16) rot=(0.57735,-0.57735,-0.57735;2.0944rad)
  _ExternalGeoVersion = 1
  sketch-geometry (4):
    g0: Circle CenterX=-19 CenterY=15.34 CenterZ=0 NormalX=0 NormalY=0 NormalZ=1 AngleXU=0 Radius=1.1
    g1: Circle CenterX=-27 CenterY=15.34 CenterZ=0 NormalX=0 NormalY=0 NormalZ=1 AngleXU=0 Radius=1.1
    g2: Circle CenterX=-19 CenterY=-6.66 CenterZ=0 NormalX=0 NormalY=0 NormalZ=1 AngleXU=0 Radius=1.1
    g3: Circle CenterX=-27 CenterY=-6.66 CenterZ=0 NormalX=0 NormalY=0 NormalZ=1 AngleXU=0 Radius=1.1
  constraints (12):
    c: Diameter(g0) = 2.2
    c: Equal(g1,g0)
    c: Equal(g3,g1)
    c: Equal(g2,g3)
    c: DistanceX(g1,g0) = 8
    c: DistanceX(g3,g2) = 8
    c: Distance(g0,g-1) = 15.34
    c: Distance(g0,g-2) = 19
    c: Distance(g1,g-1) = 15.34
    c: Distance(g2,g-2) = 19
    c: Distance(g2,g-1) = 6.66
    c: Distance(g3,g-1) = 6.66
FEATURE [PartDesign::Hole] Hole010
  BaseFeature = -> Fillet013
  BaseProfileType = 7
  CustomThreadClearance = 0
  Depth = 10
  DepthType = 0
  Diameter = 3.1
  DrillForDepth = false
  DrillPoint = 0
  DrillPointAngle = 118
  HoleCutCountersinkAngle = 90
  HoleCutCustomValues = false
  HoleCutDepth = 3
  HoleCutDiameter = 5
  HoleCutType = 1
  ModelThread = false
  Placement = pos=(0,0,19.16) rot=(0,0,1;1.5708rad)
  Profile = -> Sketch028
  Refine = true
  Suppressed = false
  Tapered = false
  TaperedAngle = 90
  ThreadClass = 0
  ThreadDepth = 10
  ThreadDepthType = 0
  ThreadDiameter = 2.5
  ThreadDirection = 0
  ThreadFit = 2
  ThreadSize = 8
  ThreadType = 1
  Threaded = false
  UseCustomThreadClearance = false
FEATURE [PartDesign::Body] Body003
  AllowCompound = true
  Group = -> [CopyPart__Feature010,Sketch022,Pad014,Sketch023,Hole008,PolarPattern001,Sketch024,Hole009,Sketch025,Pad015,Sketch026,Pad016,Sketch027,Pad017,Fillet011,Fillet012,Fillet013,Sketch028,Hole010]
  Origin = -> Origin014
  Placement = pos=(36,0,47) rot=(0,-1,0;3.14159rad)
  Tip = -> Hole010
FEATURE [App::Point] Origin017  label="Origin019"
  Role = Origin
FEATURE [Sketcher::SketchObject] Sketch029
  ArcFitTolerance = 1e-06
  AttachmentSupport = -> [Origin016]
  ExternalTypes = [0]
  FullyConstrained = true
  MakeInternals = false
  MapMode = 5
  Placement = pos=(0,0,0) rot=(0.57735,0.57735,0.57735;2.0944rad)
  _ExternalGeoVersion = 1
  sketch-geometry (5):
    g0: LineSegment StartX=-45 StartY=-7.5 StartZ=0 EndX=45 EndY=-7.5 EndZ=0
    g1: LineSegment StartX=45 StartY=-7.5 StartZ=0 EndX=45 EndY=7.5 EndZ=0
    g2: LineSegment StartX=45 StartY=7.5 StartZ=0 EndX=-45 EndY=7.5 EndZ=0
    g3: LineSegment StartX=-45 StartY=7.5 StartZ=0 EndX=-45 EndY=-7.5 EndZ=0
    g4: GeomPoint [constr] X=0 Y=0 Z=0
  constraints (12):
    c: Coincident(g0,g1)
    c: Coincident(g1,g2)
    c: Coincident(g2,g3)
    c: Coincident(g3,g0)
    c: Horizontal(g0)
    c: Horizontal(g2)
    c: Vertical(g1)
    c: Vertical(g3)
    c: Symmetric(g2,g0,g4)
    c: Distance(g1,g3) = 90
    c: Distance(g0,g2) = 15
    c: Coincident(g4,g-1)
FEATURE [PartDesign::Pad] Pad018
  Direction = (1,0,0)
  Length = 3
  Length2 = 10
  Profile = -> Sketch029
  ReferenceAxis = -> Sketch029 [N_Axis]
  Refine = true
  SideType = 0
  Suppressed = false
  Type = 0
  Type2 = 0
FEATURE [Sketcher::SketchObject] Sketch030
  ArcFitTolerance = 1e-06
  AttachmentSupport = -> [Pad018]
  ExternalGeometry = -> [Pad018]
  ExternalTypes = [0,0]
  FullyConstrained = true
  MakeInternals = false
  MapMode = 5
  Placement = pos=(0,0,0) rot=(0.57735,-0.57735,-0.57735;2.0944rad)
  _ExternalGeoVersion = 1
  sketch-geometry (4):
    g0: Circle CenterX=-11 CenterY=4 CenterZ=0 NormalX=0 NormalY=0 NormalZ=1 AngleXU=0 Radius=1.1
    g1: Circle CenterX=-11 CenterY=-4 CenterZ=0 NormalX=0 NormalY=0 NormalZ=1 AngleXU=0 Radius=1.1
    g2: Circle CenterX=11 CenterY=4 CenterZ=0 NormalX=0 NormalY=0 NormalZ=1 AngleXU=0 Radius=1.1
    g3: Circle CenterX=11 CenterY=-4 CenterZ=0 NormalX=0 NormalY=0 NormalZ=1 AngleXU=0 Radius=1.1
  constraints (12):
    c: Diameter(g0) = 2.2
    c: Equal(g0,g1)
    c: Distance(g0,g1) = 8
    c: Distance(g0,g-2) = 11
    c: Distance(g1,g-2) = 11
    c: Distance(g0,g-1) = 4
    c: Equal(g1,g3)
    c: Equal(g3,g2)
    c: Distance(g3,g-2) = 11
    c: Distance(g2,g-2) = 11
    c: Distance(g2,g-1) = 4
    c: Distance(g2,g3) = 8
FEATURE [PartDesign::Hole] Hole011
  BaseFeature = -> Pad018
  BaseProfileType = 7
  CustomThreadClearance = 0
  Depth = 3
  DepthType = 0
  Diameter = 3.1
  DrillForDepth = false
  DrillPoint = 0
  DrillPointAngle = 118
  HoleCutCountersinkAngle = 90
  HoleCutCustomValues = false
  HoleCutDepth = 2.5
  HoleCutDiameter = 5
  HoleCutType = 2
  ModelThread = false
  Profile = -> Sketch030
  Refine = true
  Suppressed = false
  Tapered = false
  TaperedAngle = 90
  ThreadClass = 0
  ThreadDepth = 3
  ThreadDepthType = 0
  ThreadDiameter = 2.5
  ThreadDirection = 0
  ThreadFit = 2
  ThreadSize = 8
  ThreadType = 1
  Threaded = false
  UseCustomThreadClearance = false
FEATURE [Sketcher::SketchObject] Sketch031
  ArcFitTolerance = 1e-06
  AttachmentSupport = -> [Hole011]
  ExternalTypes = [0]
  FullyConstrained = true
  MakeInternals = false
  MapMode = 5
  Placement = pos=(0,0,0) rot=(0.57735,-0.57735,-0.57735;2.0944rad)
  _ExternalGeoVersion = 1
  sketch-geometry (4):
    g0: LineSegment StartX=-45 StartY=7.5 StartZ=0 EndX=-45 EndY=-7.5 EndZ=0
    g1: LineSegment StartX=-45 StartY=-7.5 StartZ=0 EndX=-35 EndY=-7.5 EndZ=0
    g2: LineSegment StartX=-35 StartY=-7.5 StartZ=0 EndX=-35 EndY=7.5 EndZ=0
    g3: LineSegment StartX=-35 StartY=7.5 StartZ=0 EndX=-45 EndY=7.5 EndZ=0
  constraints (12):
    c: Coincident(g0,g1)
    c: Coincident(g1,g2)
    c: Coincident(g2,g3)
    c: Coincident(g3,g0)
    c: Vertical(g0)
    c: Vertical(g2)
    c: Horizontal(g1)
    c: Horizontal(g3)
    c: Distance(g0,g2) = 10
    c: Distance(g1,g3) = 15
    c: Distance(g-1,g3) = 7.5
    c: Distance(g-2,g0) = 45
FEATURE [PartDesign::Pad] Pad019
  BaseFeature = -> Hole011
  Direction = (-1,0,0)
  Length = 5
  Length2 = 10
  Profile = -> Sketch031
  ReferenceAxis = -> Sketch031 [N_Axis]
  Refine = true
  SideType = 0
  Suppressed = false
  Type = 0
  Type2 = 0
FEATURE [PartDesign::Body] Body004
  AllowCompound = true
  Group = -> [Sketch029,Pad018,Sketch030,Hole011,Sketch031,Pad019]
  Origin = -> Origin016
  Tip = -> Pad019
FEATURE [App::Point] Origin019  label="Origin021"
  Role = Origin
FEATURE [Sketcher::SketchObject] Sketch032
  ArcFitTolerance = 1e-06
  AttachmentSupport = -> [Origin018]
  ExternalTypes = [0]
  FullyConstrained = true
  MakeInternals = false
  MapMode = 5
  Placement = pos=(0,0,0) rot=(0.57735,0.57735,0.57735;2.0944rad)
  _ExternalGeoVersion = 1
  sketch-geometry (5):
    g0: LineSegment StartX=-45 StartY=-7.5 StartZ=0 EndX=45 EndY=-7.5 EndZ=0
    g1: LineSegment StartX=45 StartY=-7.5 StartZ=0 EndX=45 EndY=7.5 EndZ=0
    g2: LineSegment StartX=45 StartY=7.5 StartZ=0 EndX=-45 EndY=7.5 EndZ=0
    g3: LineSegment StartX=-45 StartY=7.5 StartZ=0 EndX=-45 EndY=-7.5 EndZ=0
    g4: GeomPoint [constr] X=0 Y=0 Z=0
  constraints (12):
    c: Coincident(g0,g1)
    c: Coincident(g1,g2)
    c: Coincident(g2,g3)
    c: Coincident(g3,g0)
    c: Horizontal(g0)
    c: Horizontal(g2)
    c: Vertical(g1)
    c: Vertical(g3)
    c: Symmetric(g2,g0,g4)
    c: Distance(g1,g3) = 90
    c: Distance(g0,g2) = 15
    c: Coincident(g4,g-1)
FEATURE [PartDesign::Pad] Pad020
  Direction = (1,0,0)
  Length = 3
  Length2 = 10
  Profile = -> Sketch032
  ReferenceAxis = -> Sketch032 [N_Axis]
  Refine = true
  SideType = 0
  Suppressed = false
  Type = 0
  Type2 = 0
FEATURE [Sketcher::SketchObject] Sketch033
  ArcFitTolerance = 1e-06
  AttachmentSupport = -> [Pad020]
  ExternalTypes = [0]
  FullyConstrained = true
  MakeInternals = false
  MapMode = 5
  Placement = pos=(0,0,0) rot=(0.57735,-0.57735,-0.57735;2.0944rad)
  _ExternalGeoVersion = 1
  sketch-geometry (4):
    g0: Circle CenterX=-11 CenterY=4 CenterZ=0 NormalX=0 NormalY=0 NormalZ=1 AngleXU=0 Radius=1.25
    g1: Circle CenterX=-11 CenterY=-4 CenterZ=0 NormalX=0 NormalY=0 NormalZ=1 AngleXU=0 Radius=1.25
    g2: Circle CenterX=11 CenterY=4 CenterZ=0 NormalX=0 NormalY=0 NormalZ=1 AngleXU=0 Radius=1.25
    g3: Circle CenterX=11 CenterY=-4 CenterZ=0 NormalX=0 NormalY=0 NormalZ=1 AngleXU=0 Radius=1.25
  constraints (12):
    c: Diameter(g0) = 2.5
    c: Equal(g0,g1)
    c: Equal(g1,g3)
    c: Equal(g3,g2)
    c: Distance(g0,g-1) = 4
    c: Distance(g0,g-2) = 11
    c: Distance(g1,g-2) = 11
    c: Distance(g1,g0) = 8
    c: Distance(g2,g-2) = 11
    c: Distance(g3,g-2) = 11
    c: Distance(g3,g2) = 8
    c: Distance(g2,g-1) = 4
FEATURE [PartDesign::Hole] Hole012
  BaseFeature = -> Pad020
  BaseProfileType = 7
  CustomThreadClearance = 0
  Depth = 3
  DepthType = 0
  Diameter = 3.1
  DrillForDepth = false
  DrillPoint = 0
  DrillPointAngle = 118
  HoleCutCountersinkAngle = 90
  HoleCutCustomValues = false
  HoleCutDepth = 2.95
  HoleCutDiameter = 5.9
  HoleCutType = 2
  ModelThread = false
  Profile = -> Sketch033
  Refine = true
  Suppressed = false
  Tapered = false
  TaperedAngle = 90
  ThreadClass = 0
  ThreadDepth = 3
  ThreadDepthType = 0
  ThreadDiameter = 2.5
  ThreadDirection = 0
  ThreadFit = 2
  ThreadSize = 8
  ThreadType = 1
  Threaded = false
  UseCustomThreadClearance = false
FEATURE [Sketcher::SketchObject] Sketch034
  ArcFitTolerance = 1e-06
  AttachmentSupport = -> [Hole012]
  ExternalTypes = [0]
  FullyConstrained = true
  MakeInternals = false
  MapMode = 5
  Placement = pos=(0,0,0) rot=(0.57735,-0.57735,-0.57735;2.0944rad)
  _ExternalGeoVersion = 1
  sketch-geometry (4):
    g0: LineSegment StartX=45 StartY=7.5 StartZ=0 EndX=35 EndY=7.5 EndZ=0
    g1: LineSegment StartX=35 StartY=7.5 StartZ=0 EndX=35 EndY=-7.5 EndZ=0
    g2: LineSegment StartX=35 StartY=-7.5 StartZ=0 EndX=45 EndY=-7.5 EndZ=0
    g3: LineSegment StartX=45 StartY=-7.5 StartZ=0 EndX=45 EndY=7.5 EndZ=0
  constraints (12):
    c: Coincident(g0,g1)
    c: Coincident(g1,g2)
    c: Coincident(g2,g3)
    c: Coincident(g3,g0)
    c: Horizontal(g0)
    c: Horizontal(g2)
    c: Vertical(g1)
    c: Vertical(g3)
    c: Distance(g1,g3) = 10
    c: Distance(g0,g2) = 15
    c: Distance(g-2,g1) = 35
    c: Distance(g-1,g0) = 7.5
FEATURE [PartDesign::Pocket] Pocket
  BaseFeature = -> Hole012
  Direction = (1,0,0)
  Length = 3
  Length2 = 5
  Profile = -> Sketch034
  ReferenceAxis = -> Sketch034 [N_Axis]
  Refine = true
  SideType = 0
  Suppressed = false
  Type = 0
  Type2 = 0
FEATURE [PartDesign::Body] Body005
  AllowCompound = true
  Group = -> [Sketch032,Pad020,Sketch033,Hole012,Sketch034,Pocket]
  Origin = -> Origin018
  Tip = -> Pocket
FEATURE [App::Point] Origin021  label="Origin024"
  Role = Origin
FEATURE [App::Link] Body006
  LinkPlacement = pos=(36,-8.06848e-06,-0.499997) rot=(1,0,0;3.14159rad)
  LinkedObject = -> Body002
  Placement = pos=(36,-8.06848e-06,-0.499997) rot=(1,0,0;3.14159rad)
FEATURE [App::FeaturePython] GroundedJoint  # Assembly grounded joint (typed FeaturePython)
  ObjectToGround = -> Body006
FEATURE [App::Link] ASM0001_ASM002
  LinkPlacement = pos=(72,-1.67271e-05,3.27024e-06) rot=(0,0,1;3.14159rad)
  LinkedObject = -> ASM0001_ASM001
  Placement = pos=(72,-1.67271e-05,3.27024e-06) rot=(0,0,1;3.14159rad)
FEATURE [App::Link] ASM0001_ASM003
  LinkPlacement = pos=(36,-8.14398e-06,3.27024e-06) rot=(0,0,1;3.14159rad)
  LinkedObject = -> ASM0001_ASM001
  Placement = pos=(36,-8.14398e-06,3.27024e-06) rot=(0,0,1;3.14159rad)
FEATURE [App::FeaturePython] Joint  label="Fixed"  # Assembly joint (typed FeaturePython)
  Angle = 0
  AngleMax = 0
  AngleMin = 0
  Detach1 = false
  Detach2 = false
  Distance = 0
  Distance2 = 0
  EnableAngleMax = false
  EnableAngleMin = false
  EnableLengthMax = false
  EnableLengthMin = false
  JointType = 0 (Fixed)
  LengthMax = 0
  LengthMin = 0
  Offset2 = pos=(0,0,0) rot=(0,0,-1;1.5708rad)
  Placement1 = pos=(13.5,-14.5,16) rot=(0,0,1;1.5708rad)
  Placement2 = pos=(-13.5,-14.5,-16.5) rot=(-0.707107,-0.707107,0;3.14159rad)
  Reference1 = -> ASM0001_ASM003 [ASM0002_ASM001.Part__Feature011.Edge800,ASM0002_ASM001.Part__Feature011.Edge800]
  Reference2 = -> Body006 [Edge112,Edge112]
  Suppressed = false
FEATURE [App::FeaturePython] Joint001  label="Fixed001"  # Assembly joint (typed FeaturePython)
  Angle = 0
  AngleMax = 0
  AngleMin = 0
  Detach1 = false
  Detach2 = false
  Distance = 0
  Distance2 = 0
  EnableAngleMax = false
  EnableAngleMin = false
  EnableLengthMax = false
  EnableLengthMin = false
  JointType = 0 (Fixed)
  LengthMax = 0
  LengthMin = 0
  Offset2 = pos=(0,0,0) rot=(0,0,-1;1.5708rad)
  Placement1 = pos=(-13.5,-14.5,16) rot=(0,0,1;1.5708rad)
  Placement2 = pos=(49.5,-14.5,-16.5) rot=(-0.707107,-0.707107,0;3.14159rad)
  Reference1 = -> ASM0001_ASM002 [ASM0002_ASM001.Part__Feature011.Edge812,ASM0002_ASM001.Part__Feature011.Edge812]
  Reference2 = -> Body006 [Edge107,Edge107]
  Suppressed = false
FEATURE [App::Link] Body007
  LinkPlacement = pos=(72,-1.67271e-05,3.27024e-06) rot=(0,0,1;3.1705rad)
  LinkedObject = -> Body
  Placement = pos=(72,-1.67271e-05,3.27024e-06) rot=(0,0,1;3.1705rad)
FEATURE [App::FeaturePython] Joint002  label="Revolute003"  # Assembly joint (typed FeaturePython)
  Angle = 0
  AngleMax = 0
  AngleMin = 0
  Detach1 = false
  Detach2 = false
  Distance = 0
  Distance2 = 0
  EnableAngleMax = false
  EnableAngleMin = false
  EnableLengthMax = false
  EnableLengthMin = false
  JointType = 1 (Revolute)
  LengthMax = 0
  LengthMin = 0
  Placement1 = pos=(0,0,1.84) rot=(0,0,-1;1.5708rad)
  Placement2 = pos=(1.42e-14,-4e-16,21) rot=(0,0,-1;4.71239rad)
  Reference1 = -> ASM0001_ASM002 [ASM0002_ASM001.Part__Feature020.Edge126,ASM0002_ASM001.Part__Feature020.Edge126]
  Reference2 = -> Body007 [Edge16,Edge16]
  Suppressed = false
FEATURE [App::Link] Body008
  LinkPlacement = pos=(36,-1.52408e-05,47) rot=(0.999864,0.01647,0;3.14159rad)
  LinkedObject = -> Body
  Placement = pos=(36,-1.52408e-05,47) rot=(0.999864,0.01647,0;3.14159rad)
FEATURE [App::FeaturePython] Joint003  label="Revolute004"  # Assembly joint (typed FeaturePython)
  Angle = 0
  AngleMax = 0
  AngleMin = 0
  Detach1 = false
  Detach2 = false
  Distance = 0
  Distance2 = 0
  EnableAngleMax = false
  EnableAngleMin = false
  EnableLengthMax = false
  EnableLengthMin = false
  JointType = 1 (Revolute)
  LengthMax = 0
  LengthMin = 0
  Placement1 = pos=(0,0,1.84) rot=(0,0,1;0rad)
  Placement2 = pos=(0,0,26) rot=(0,0,-1;4.71239rad)
  Reference1 = -> ASM0001_ASM003 [ASM0002_ASM001.Part__Feature020.Edge123,ASM0002_ASM001.Part__Feature020.Edge123]
  Reference2 = -> Body008 [Edge53,Edge53]
  Suppressed = false
FEATURE [App::Link] Body009
  LinkPlacement = pos=(53.7483,-22.4276,23.5) rot=(-0.011647,0.707059,0.707059;3.16488rad)
  LinkedObject = -> Body005
  Placement = pos=(53.7483,-22.4276,23.5) rot=(-0.011647,0.707059,0.707059;3.16488rad)
FEATURE [App::FeaturePython] Joint004  label="Fixed003"  # Assembly joint (typed FeaturePython)
  Angle = 0
  AngleMax = 0
  AngleMin = 0
  Detach1 = false
  Detach2 = false
  Distance = 0
  Distance2 = 0
  EnableAngleMax = false
  EnableAngleMin = false
  EnableLengthMax = false
  EnableLengthMin = false
  JointType = 0 (Fixed)
  LengthMax = 0
  LengthMin = 0
  Offset2 = pos=(0,0,0) rot=(0,0,-1;3.14159rad)
  Placement1 = pos=(3,11,4) rot=(0,-1,0;1.5708rad)
  Placement2 = pos=(14,19,12.5) rot=(-0.57735,0.57735,0.57735;4.18879rad)
  Reference1 = -> Body009 [Edge17,Edge17]
  Reference2 = -> Body008 [Edge82,Edge82]
  Suppressed = false
FEATURE [App::Link] Body010
  LinkPlacement = pos=(55.6718,-23.4817,23.5) rot=(-0.999791,-0.01445,0.01445;1.571rad)
  LinkedObject = -> Body004
  Placement = pos=(55.6718,-23.4817,23.5) rot=(-0.999791,-0.01445,0.01445;1.571rad)
FEATURE [App::FeaturePython] Joint005  label="Fixed004"  # Assembly joint (typed FeaturePython)
  Angle = 0
  AngleMax = 0
  AngleMin = 0
  Detach1 = false
  Detach2 = false
  Distance = 0
  Distance2 = 0
  EnableAngleMax = false
  EnableAngleMin = false
  EnableLengthMax = false
  EnableLengthMin = false
  JointType = 0 (Fixed)
  LengthMax = 0
  LengthMin = 0
  Offset2 = pos=(0,0,0) rot=(0,0,-1;3.14159rad)
  Placement1 = pos=(14,19,34.5) rot=(0.57735,0.57735,-0.57735;4.18879rad)
  Placement2 = pos=(3,-11,4) rot=(-0.707107,0,0.707107;3.14159rad)
  Reference1 = -> Body007 [Edge81,Edge81]
  Reference2 = -> Body010 [Edge18,Edge18]
  Suppressed = false
FEATURE [Assembly::JointGroup] Joints
  Group = -> [GroundedJoint,Joint,Joint001,Joint002,Joint003,Joint004,Joint005]
FEATURE [App::Link] Body011
  LinkPlacement = pos=(53.5,-47,23.5) rot=(0,1,0;1.5708rad)
  LinkedObject = -> <external ../card/Unnamed1.FCStd>#Body
  Placement = pos=(53.5,-47,23.5) rot=(0,1,0;1.5708rad)
FEATURE [Assembly::AssemblyObject] Assembly
  Group = -> [Joints,Body006,GroundedJoint,ASM0001_ASM002,ASM0001_ASM003,Joint,Joint001,Body007,Joint002,Body008,Joint003,Body009,Joint004,Body010,Joint005,Body011]
  Origin = -> Origin020
  Type = Assembly

RESOLVED EXTERNAL PARTS (link-assembly join: the EXTERNAL_REF files above that resolve inside this repo's crawl, each included once):
---- part ../card/Unnamed1.FCStd = doc fcstd_ffb08756d0cd ----
FCSTD DOCUMENT  (FreeCAD 1.1R20260414 (Git shallow))
Label: Unnamed1
License: All rights reserved
LicenseURL: https://en.wikipedia.org/wiki/All_rights_reserved
objects: App::Point×1, Sketcher::SketchObject×1, PartDesign::Pad×1, PartDesign::Fillet×1, PartDesign::Body×1
note: 9 computed .brp shape members not serialized (recipe doc carries the construction recipe); baked Part::Feature solids carry a one-line shape summary decoded from their .brp

FEATURE [App::Point] Origin001
  Role = Origin
FEATURE [Sketcher::SketchObject] Sketch
  ArcFitTolerance = 1e-06
  AttachmentSupport = -> [Origin]
  ExternalTypes = [0]
  FullyConstrained = true
  MakeInternals = false
  MapMode = 5
  _ExternalGeoVersion = 1
  sketch-geometry (5):
    g0: LineSegment StartX=-42.5 StartY=-27 StartZ=0 EndX=42.5 EndY=-27 EndZ=0
    g1: LineSegment StartX=42.5 StartY=-27 StartZ=0 EndX=42.5 EndY=27 EndZ=0
    g2: LineSegment StartX=42.5 StartY=27 StartZ=0 EndX=-42.5 EndY=27 EndZ=0
    g3: LineSegment StartX=-42.5 StartY=27 StartZ=0 EndX=-42.5 EndY=-27 EndZ=0
    g4: GeomPoint [constr] X=0 Y=0 Z=0
  constraints (12):
    c: Coincident(g0,g1)
    c: Coincident(g1,g2)
    c: Coincident(g2,g3)
    c: Coincident(g3,g0)
    c: Horizontal(g0)
    c: Horizontal(g2)
    c: Vertical(g1)
    c: Vertical(g3)
    c: Symmetric(g2,g0,g4)
    c: Distance(g1,g3) = 85
    c: Distance(g0,g2) = 54
    c: Coincident(g4,g-1)
FEATURE [PartDesign::Pad] Pad
  Direction = (0,0,1)
  Length = 1
  Length2 = 10
  Profile = -> Sketch
  ReferenceAxis = -> Sketch [N_Axis]
  Refine = true
  SideType = 0
  Suppressed = false
  Type = 0
  Type2 = 0
FEATURE [PartDesign::Fillet] Fillet
  Base = -> Pad [Edge2,Edge5,Edge8,Edge1]
  BaseFeature = -> Pad
  Radius = 1.5
  Refine = true
  SupportTransform = false
  Suppressed = false
  UseAllEdges = false
FEATURE [PartDesign::Body] Body
  AllowCompound = true
  Group = -> [Sketch,Pad,Fillet]
  Origin = -> Origin
  Tip = -> Fillet
